# Revit family: Haworth_XSeries_PersonalStorageTower_15Wide56High
name_source: partatom
category: Furniture Systems
units: mm (PartAtom-declared; Revit-internal decimal feet)

## family parameters
Always vertical = Yes
Cut with Voids When Loaded = No
OmniClass Number = 23.40.70.14.64.21
OmniClass Title = Systems Furniture
Part Type = Normal
Room Calculation Point = No
Round Connector Dimension = Use Diameter
Shared = No
Work Plane-Based = No

## types (5) — shared parameters
Actual Depth = 23 5/8"
Actual Height = 56 1/2"
Actual Width = 15"
Assembly Code = E2020200
Classic Pull = No
Crescent Pull = No
Description = Haworth XSeries Personal Storage Tower
Drawer 1 Height = 12"
Drawer 3 Height = 5 15/16"
Drawer Width = 14 7/8"
Ellipse Pull = No
J Pull = No
Linear Pull = Yes
Manufacturer = Haworth
Model = J2HD-5615
Pull Finish = Haworth _ Metal _ Brushed Aluminum
Radius Pull = No
Revision Number = 3
Shelf Depth = 13 1/2"
Shelf Width = 22 1/8"
Size = Verify Final Dim. w/ Haworth
Standard Heights = 56.5 in.
Sustainability Info = https://www.haworth.com
Taper Pull = No
URL = http://www.haworth.com
URL - Product = https://www.haworth.com
Warranty = https://cdn.shopify.com

## per-type parameters (varying)
| type | Box Box File | Box File | Door Height 2 | Drawer 2 Height | Drawer 3 | File File | Pull Height Centerline 2 | Top Height | Upper Bookcase | Upper Door |
| 24d 15w 56h - Upper Door - File File | No | No | 27 1/2" | 12" | No | Yes | 13 3/4" | 29" | No | Yes |
| 24d 15w 56h - Upper Door - Box Box File | Yes | No | 27 1/2" | 5 15/16" | Yes | No | 13 3/4" | 29" | No | Yes |
| 24d 15w 56h - Upper Door - Box File | No | Yes | 33 9/16" | 5 15/16" | No | No | 16 25/32" | 35 1/16" | No | Yes |
| 24d 15w 56h - Upper Bookcase - File File | No | No | 27 1/2" | 12" | No | Yes | 13 3/4" | 29" | Yes | No |
| 24d 15w 56h - Upper Bookcase - Box Box File | Yes | No | 27 1/2" | 5 15/16" | Yes | No | 13 3/4" | 29" | Yes | No |

## geometry (parser evidence)
native form markers: Sweep x12
no freeform markers — native parametric forms only
